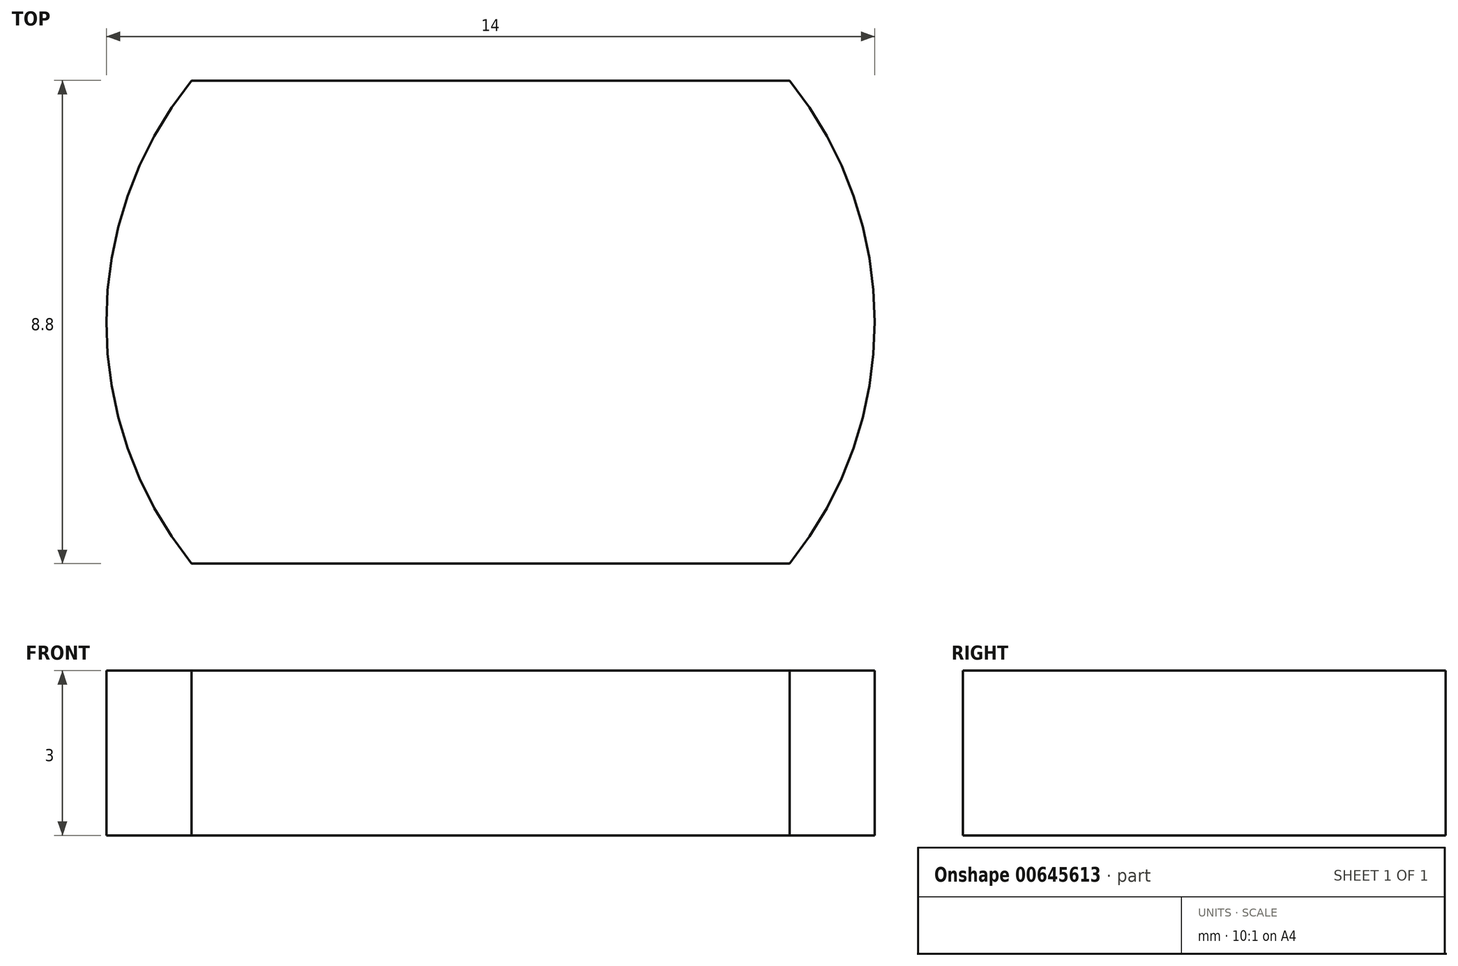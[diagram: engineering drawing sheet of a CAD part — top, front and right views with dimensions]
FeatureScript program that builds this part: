
annotation { "Feature Type Name" : "Feature", "Feature Type Description" : "" }
export const myFeature = defineFeature(function(context is Context, id is Id, definition is map)
    precondition{}
    {
        {
            var Q0;
            Q0=qCreatedBy(makeId("Top.planeOp"),FACE);
            var sketch = newSketch(context, id + "F0", { "sketchPlane" : qUnion([Q0])});
            skArc(sketch, "E0", {"start": v(-5.45, 4.4) * mm, "mid": v(-7, 0) * mm, "end": v(-5.45, -4.4) * mm});
            skLineSegment(sketch, "E1", {"start": v(-5.45, 4.4) * mm, "end": v(5.45, 4.4) * mm});
            skLineSegment(sketch, "E2.MirrorCS", {"start": v(-5.45, -4.4) * mm, "end": v(5.45, -4.4) * mm});
            skArc(sketch, "E3.trimOffspring", {"start": v(5.45, -4.4) * mm, "mid": v(7, 0) * mm, "end": v(5.45, 4.4) * mm});
            skPoint(sketch, "E4", {"position": v(-4.79, 0) * mm});
            skPoint(sketch, "E5", {"position": v(4.77, 0) * mm});
            skSolve(sketch);
        }
        {
            var Q0;
            Q0 = qSketchRegion(id + "F0", true);
            extrude(context, id + "F1", {"entities" : qUnion([Q0]), "depth" : 3 * mm, "offsetDistance" : 25 * mm});
        }
    });
